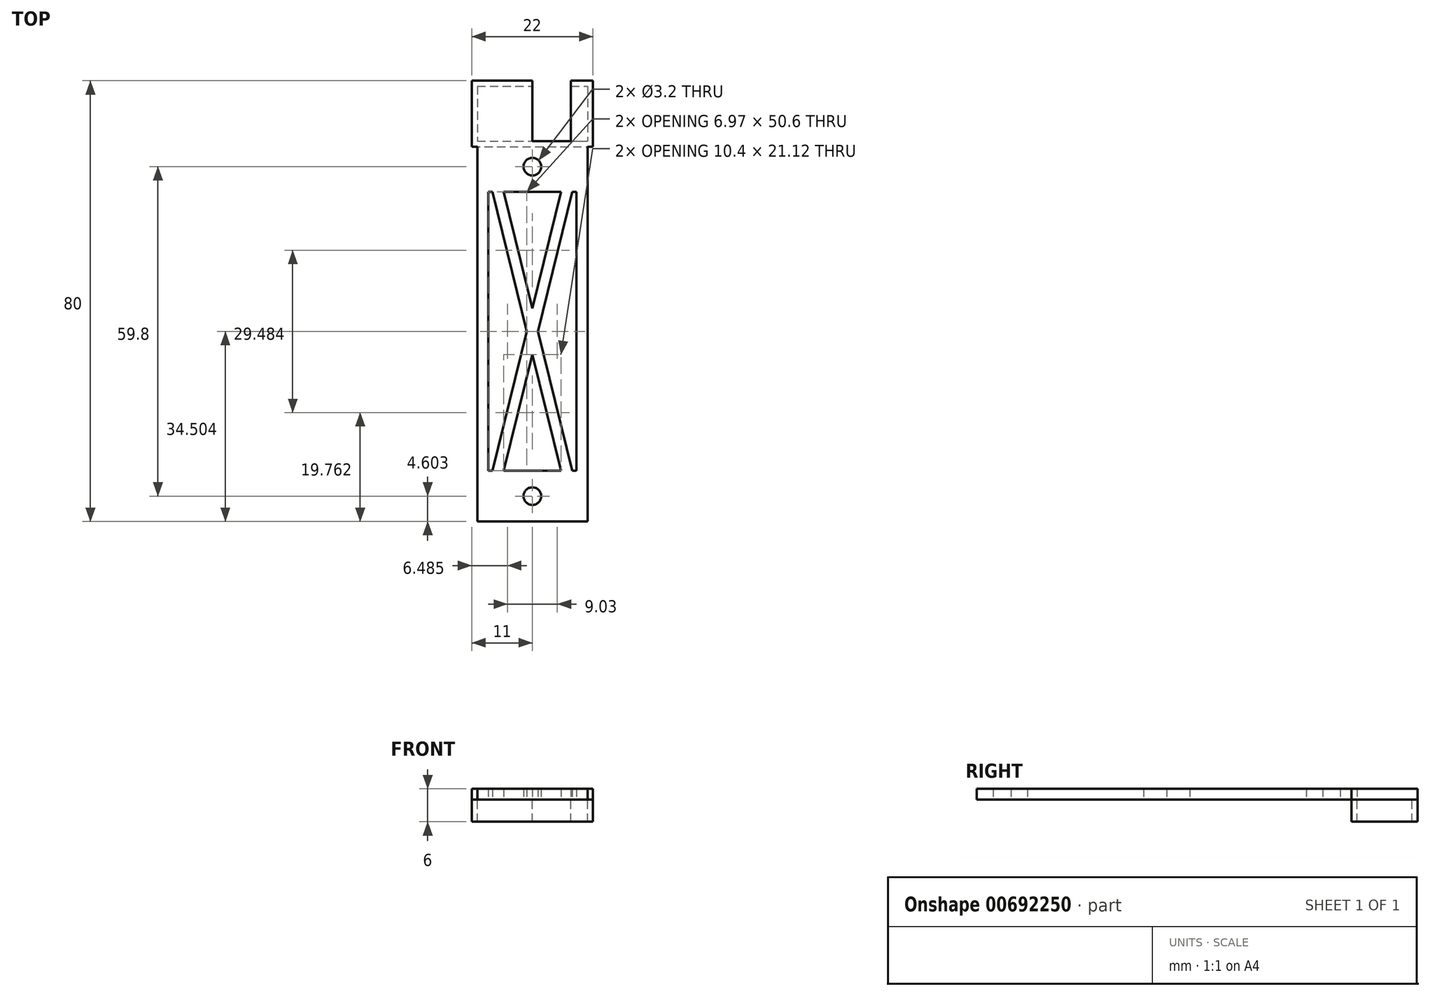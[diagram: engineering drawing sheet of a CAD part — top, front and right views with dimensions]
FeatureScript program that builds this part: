
annotation { "Feature Type Name" : "Feature", "Feature Type Description" : "" }
export const myFeature = defineFeature(function(context is Context, id is Id, definition is map)
    precondition{}
    {
        {
            var Q0;
            Q0=qCreatedBy(makeId("Top.planeOp"),FACE);
            var sketch = newSketch(context, id + "F0", { "sketchPlane" : qUnion([Q0])});
            skLineSegment(sketch, "E0.bottom", {"start": v(-16.97, 32.6) * mm, "end": v(3.03, 32.6) * mm});
            skLineSegment(sketch, "E0.top", {"start": v(-16.97, -47.4) * mm, "end": v(3.03, -47.4) * mm});
            skLineSegment(sketch, "E0.left", {"start": v(-16.97, 32.6) * mm, "end": v(-16.97, -47.4) * mm});
            skLineSegment(sketch, "E0.right", {"start": v(3.03, 32.6) * mm, "end": v(3.03, -47.4) * mm});
            skLineSegment(sketch, "E1", {"start": v(-6.97, 32.6) * mm, "end": v(-6.97, -47.4) * mm});
            skCircle(sketch, "E2", {"center": v(-6.97, -42.8) * mm, "radius": 1.6 * mm});
            skCircle(sketch, "E3", {"center": v(-6.97, 17) * mm, "radius": 1.6 * mm});
            skLineSegment(sketch, "E4", {"start": v(-16.97, 21.6) * mm, "end": v(3.03, 21.6) * mm});
            skLineSegment(sketch, "E5", {"start": v(-16.97, 31.6) * mm, "end": v(3.03, 31.6) * mm});
            skLineSegment(sketch, "E6", {"start": v(-16.97, 20.6) * mm, "end": v(3.03, 20.6) * mm});
            skLineSegment(sketch, "E7", {"start": v(-16.97, 32.6) * mm, "end": v(-17.97, 32.6) * mm});
            skLineSegment(sketch, "E8", {"start": v(-16.97, 20.6) * mm, "end": v(-17.97, 20.6) * mm});
            skLineSegment(sketch, "E9", {"start": v(-17.97, 32.6) * mm, "end": v(-17.97, 20.6) * mm});
            skLineSegment(sketch, "E10", {"start": v(3.03, 32.6) * mm, "end": v(4.03, 32.6) * mm});
            skLineSegment(sketch, "E11", {"start": v(3.03, 20.6) * mm, "end": v(4.03, 20.6) * mm});
            skLineSegment(sketch, "E12", {"start": v(4.03, 32.6) * mm, "end": v(4.03, 20.6) * mm});
            skLineSegment(sketch, "E13", {"start": v(0.03, 32.6) * mm, "end": v(0.03, 21.6) * mm});
            skLineSegment(sketch, "E14", {"start": v(-14.97, 19.6) * mm, "end": v(-14.97, -45.4) * mm});
            skLineSegment(sketch, "E15", {"start": v(-14.97, -45.4) * mm, "end": v(1.03, -45.4) * mm});
            skLineSegment(sketch, "E16", {"start": v(1.03, -45.4) * mm, "end": v(1.03, 19.6) * mm});
            skLineSegment(sketch, "E17", {"start": v(1.03, 19.6) * mm, "end": v(-14.97, 19.6) * mm});
            skLineSegment(sketch, "E18", {"start": v(-14.97, 19.6) * mm, "end": v(1.03, -45.4) * mm});
            skLineSegment(sketch, "E19", {"start": v(1.03, 19.6) * mm, "end": v(-14.97, -45.4) * mm});
            skLineSegment(sketch, "E20", {"start": v(-13.94, 19.6) * mm, "end": v(1.03, -41.21) * mm});
            skLineSegment(sketch, "E21", {"start": v(-14.97, 15.42) * mm, "end": v(0, -45.4) * mm});
            skLineSegment(sketch, "E22", {"start": v(0, 19.6) * mm, "end": v(-14.97, -41.21) * mm});
            skLineSegment(sketch, "E23", {"start": v(1.03, 15.42) * mm, "end": v(-13.94, -45.4) * mm});
            skLineSegment(sketch, "E24", {"start": v(-14.97, -38.2) * mm, "end": v(1.03, -38.2) * mm});
            skLineSegment(sketch, "E25", {"start": v(-14.97, 12.4) * mm, "end": v(1.03, 12.4) * mm});
            skSolve(sketch);
        }
        {
            var Q0;
            {var subQ1=sQuery(id+"F0.wireOp",EDGE,"E0.bottom");var subQ3=sQuery(id+"F0.wireOp",EDGE,"E1");var subQ4=makeQuery(id+"F0.imprint","INTERSECT",VERTEX,{"derivedFrom":[subQ1,subQ3]});Q0=makeQuery(id+"F0.imprint","IMPRINT",FACE,{"disambiguationData":[TD([[makeQuery(id+"F0.imprint","IMPRINT",EDGE,{"disambiguationData":[TD([[subQ4,-1.0]])],"derivedFrom":subQ3}),-1.0]])]});}
            var Q1;
            {var subQ0=sQuery(id+"F0.wireOp",EDGE,"E0.right");var subQ5=sQuery(id+"F0.wireOp",EDGE,"E5");var subQ6=makeQuery(id+"F0.imprint","INTERSECT",VERTEX,{"derivedFrom":[subQ0,subQ5]});Q1=makeQuery(id+"F0.imprint","IMPRINT",FACE,{"disambiguationData":[TD([[makeQuery(id+"F0.imprint","IMPRINT",EDGE,{"disambiguationData":[TD([[subQ6,1.0]])],"derivedFrom":subQ5}),1.0]])]});}
            var Q2;
            {var subQ0=sQuery(id+"F0.wireOp",EDGE,"E7");Q2=makeQuery(id+"F0.imprint","IMPRINT",FACE,{"disambiguationData":[TD([[makeQuery(id+"F0.imprint","IMPRINT",EDGE,{"derivedFrom":subQ0}),1.0]])]});}
            var Q3;
            {var subQ0=sQuery(id+"F0.wireOp",EDGE,"E10");Q3=makeQuery(id+"F0.imprint","IMPRINT",FACE,{"disambiguationData":[TD([[makeQuery(id+"F0.imprint","IMPRINT",EDGE,{"derivedFrom":subQ0}),-1.0]])]});}
            var Q4;
            {var subQ8=sQuery(id+"F0.wireOp",EDGE,"E0.left");var subQ9=sQuery(id+"F0.wireOp",EDGE,"E0.top");var subQ10=makeQuery(id+"F0.imprint","INTERSECT",VERTEX,{"derivedFrom":[subQ9,subQ8]});Q4=makeQuery(id+"F0.imprint","IMPRINT",FACE,{"disambiguationData":[TD([[makeQuery(id+"F0.imprint","IMPRINT",EDGE,{"disambiguationData":[TD([[subQ10,-1.0]])],"derivedFrom":subQ9}),1.0]])]});}
            var Q5;
            {var subQ8=sQuery(id+"F0.wireOp",EDGE,"E0.right");var subQ9=sQuery(id+"F0.wireOp",EDGE,"E0.top");var subQ10=makeQuery(id+"F0.imprint","INTERSECT",VERTEX,{"derivedFrom":[subQ9,subQ8]});Q5=makeQuery(id+"F0.imprint","IMPRINT",FACE,{"disambiguationData":[TD([[makeQuery(id+"F0.imprint","IMPRINT",EDGE,{"disambiguationData":[TD([[subQ10,1.0]])],"derivedFrom":subQ9}),1.0]])]});}
            var Q6;
            {var subQ0=sQuery(id+"F0.wireOp",EDGE,"E4");var subQ5=sQuery(id+"F0.wireOp",EDGE,"E1");var subQ6=makeQuery(id+"F0.imprint","INTERSECT",VERTEX,{"derivedFrom":[subQ5,subQ0]});Q6=makeQuery(id+"F0.imprint","IMPRINT",FACE,{"disambiguationData":[TD([[makeQuery(id+"F0.imprint","IMPRINT",EDGE,{"disambiguationData":[TD([[subQ6,-1.0]])],"derivedFrom":subQ5}),-1.0]])]});}
            var Q7;
            {var subQ0=sQuery(id+"F0.wireOp",EDGE,"E4");var subQ4=sQuery(id+"F0.wireOp",EDGE,"E1");var subQ5=makeQuery(id+"F0.imprint","INTERSECT",VERTEX,{"derivedFrom":[subQ4,subQ0]});Q7=makeQuery(id+"F0.imprint","IMPRINT",FACE,{"disambiguationData":[TD([[makeQuery(id+"F0.imprint","IMPRINT",EDGE,{"disambiguationData":[TD([[subQ5,-1.0]])],"derivedFrom":subQ4}),1.0]])]});}
            var Q8;
            {var subQ0=sQuery(id+"F0.wireOp",EDGE,"E4");var subQ1=sQuery(id+"F0.wireOp",EDGE,"E0.left");var subQ2=makeQuery(id+"F0.imprint","INTERSECT",VERTEX,{"derivedFrom":[subQ1,subQ0]});Q8=makeQuery(id+"F0.imprint","IMPRINT",FACE,{"disambiguationData":[TD([[makeQuery(id+"F0.imprint","IMPRINT",EDGE,{"disambiguationData":[TD([[subQ2,1.0]])],"derivedFrom":subQ1}),1.0]])]});}
            var Q9;
            {var subQ0=sQuery(id+"F0.wireOp",EDGE,"E4");var subQ1=sQuery(id+"F0.wireOp",EDGE,"E0.right");var subQ2=makeQuery(id+"F0.imprint","INTERSECT",VERTEX,{"derivedFrom":[subQ1,subQ0]});Q9=makeQuery(id+"F0.imprint","IMPRINT",FACE,{"disambiguationData":[TD([[makeQuery(id+"F0.imprint","IMPRINT",EDGE,{"disambiguationData":[TD([[subQ2,1.0]])],"derivedFrom":subQ1}),-1.0]])]});}
            var Q10;
            {var subQ1=sQuery(id+"F0.wireOp",EDGE,"E14");var subQ3=sQuery(id+"F0.wireOp",EDGE,"E21");var subQ4=makeQuery(id+"F0.imprint","INTERSECT",VERTEX,{"derivedFrom":[subQ1,subQ3]});Q10=makeQuery(id+"F0.imprint","IMPRINT",FACE,{"disambiguationData":[TD([[makeQuery(id+"F0.imprint","IMPRINT",EDGE,{"disambiguationData":[TD([[subQ4,-1.0]])],"derivedFrom":subQ3}),1.0]])]});}
            var Q11;
            {var subQ1=sQuery(id+"F0.wireOp",EDGE,"E17");var subQ3=sQuery(id+"F0.wireOp",EDGE,"E20");var subQ4=makeQuery(id+"F0.imprint","INTERSECT",VERTEX,{"derivedFrom":[subQ1,subQ3]});Q11=makeQuery(id+"F0.imprint","IMPRINT",FACE,{"disambiguationData":[TD([[makeQuery(id+"F0.imprint","IMPRINT",EDGE,{"disambiguationData":[TD([[subQ4,-1.0]])],"derivedFrom":subQ1}),1.0]])]});}
            var Q12;
            {var subQ1=sQuery(id+"F0.wireOp",EDGE,"E17");var subQ3=sQuery(id+"F0.wireOp",EDGE,"E22");var subQ4=makeQuery(id+"F0.imprint","INTERSECT",VERTEX,{"derivedFrom":[subQ1,subQ3]});Q12=makeQuery(id+"F0.imprint","IMPRINT",FACE,{"disambiguationData":[TD([[makeQuery(id+"F0.imprint","IMPRINT",EDGE,{"disambiguationData":[TD([[subQ4,1.0]])],"derivedFrom":subQ1}),1.0]])]});}
            var Q13;
            {var subQ0=sQuery(id+"F0.wireOp",EDGE,"E19");var subQ5=sQuery(id+"F0.wireOp",EDGE,"E20");var subQ6=makeQuery(id+"F0.imprint","INTERSECT",VERTEX,{"derivedFrom":[subQ0,subQ5]});Q13=makeQuery(id+"F0.imprint","IMPRINT",FACE,{"disambiguationData":[TD([[makeQuery(id+"F0.imprint","IMPRINT",EDGE,{"disambiguationData":[TD([[subQ6,-1.0]])],"derivedFrom":subQ5}),1.0]])]});}
            var Q14;
            {var subQ0=sQuery(id+"F0.wireOp",EDGE,"E19");var subQ5=sQuery(id+"F0.wireOp",EDGE,"E21");var subQ6=makeQuery(id+"F0.imprint","INTERSECT",VERTEX,{"derivedFrom":[subQ0,subQ5]});Q14=makeQuery(id+"F0.imprint","IMPRINT",FACE,{"disambiguationData":[TD([[makeQuery(id+"F0.imprint","IMPRINT",EDGE,{"disambiguationData":[TD([[subQ6,1.0]])],"derivedFrom":subQ5}),-1.0]])]});}
            var Q15;
            {var subQ1=sQuery(id+"F0.wireOp",EDGE,"E15");var subQ3=sQuery(id+"F0.wireOp",EDGE,"E23");var subQ4=makeQuery(id+"F0.imprint","INTERSECT",VERTEX,{"derivedFrom":[subQ1,subQ3]});Q15=makeQuery(id+"F0.imprint","IMPRINT",FACE,{"disambiguationData":[TD([[makeQuery(id+"F0.imprint","IMPRINT",EDGE,{"disambiguationData":[TD([[subQ4,1.0]])],"derivedFrom":subQ1}),1.0]])]});}
            var Q16;
            {var subQ3=sQuery(id+"F0.wireOp",EDGE,"E19");var subQ5=sQuery(id+"F0.wireOp",EDGE,"E21");var subQ6=makeQuery(id+"F0.imprint","INTERSECT",VERTEX,{"derivedFrom":[subQ3,subQ5]});Q16=makeQuery(id+"F0.imprint","IMPRINT",FACE,{"disambiguationData":[TD([[makeQuery(id+"F0.imprint","IMPRINT",EDGE,{"disambiguationData":[TD([[subQ6,1.0]])],"derivedFrom":subQ5}),1.0]])]});}
            var Q17;
            {var subQ0=sQuery(id+"F0.wireOp",EDGE,"E19");var subQ3=sQuery(id+"F0.wireOp",EDGE,"E21");var subQ5=makeQuery(id+"F0.imprint","INTERSECT",VERTEX,{"derivedFrom":[subQ0,subQ3]});Q17=makeQuery(id+"F0.imprint","IMPRINT",FACE,{"disambiguationData":[TD([[makeQuery(id+"F0.imprint","IMPRINT",EDGE,{"disambiguationData":[TD([[subQ5,1.0]])],"derivedFrom":subQ0}),1.0]])]});}
            var Q18;
            {var subQ3=sQuery(id+"F0.wireOp",EDGE,"E19");var subQ5=sQuery(id+"F0.wireOp",EDGE,"E20");var subQ6=makeQuery(id+"F0.imprint","INTERSECT",VERTEX,{"derivedFrom":[subQ3,subQ5]});Q18=makeQuery(id+"F0.imprint","IMPRINT",FACE,{"disambiguationData":[TD([[makeQuery(id+"F0.imprint","IMPRINT",EDGE,{"disambiguationData":[TD([[subQ6,-1.0]])],"derivedFrom":subQ5}),-1.0]])]});}
            var Q19;
            {var subQ0=sQuery(id+"F0.wireOp",EDGE,"E20");var subQ3=sQuery(id+"F0.wireOp",EDGE,"E19");var subQ5=makeQuery(id+"F0.imprint","INTERSECT",VERTEX,{"derivedFrom":[subQ3,subQ0]});Q19=makeQuery(id+"F0.imprint","IMPRINT",FACE,{"disambiguationData":[TD([[makeQuery(id+"F0.imprint","IMPRINT",EDGE,{"disambiguationData":[TD([[subQ5,-1.0]])],"derivedFrom":subQ3}),-1.0]])]});}
            var Q20;
            {var subQ0=sQuery(id+"F0.wireOp",EDGE,"E18");var subQ3=sQuery(id+"F0.wireOp",EDGE,"E23");var subQ5=makeQuery(id+"F0.imprint","INTERSECT",VERTEX,{"derivedFrom":[subQ0,subQ3]});Q20=makeQuery(id+"F0.imprint","IMPRINT",FACE,{"disambiguationData":[TD([[makeQuery(id+"F0.imprint","IMPRINT",EDGE,{"disambiguationData":[TD([[subQ5,1.0]])],"derivedFrom":subQ0}),-1.0]])]});}
            var Q21;
            {var subQ0=sQuery(id+"F0.wireOp",EDGE,"E22");var subQ3=sQuery(id+"F0.wireOp",EDGE,"E18");var subQ5=makeQuery(id+"F0.imprint","INTERSECT",VERTEX,{"derivedFrom":[subQ3,subQ0]});Q21=makeQuery(id+"F0.imprint","IMPRINT",FACE,{"disambiguationData":[TD([[makeQuery(id+"F0.imprint","IMPRINT",EDGE,{"disambiguationData":[TD([[subQ5,-1.0]])],"derivedFrom":subQ3}),1.0]])]});}
            var Q22;
            {var subQ1=sQuery(id+"F0.wireOp",EDGE,"E16");var subQ3=sQuery(id+"F0.wireOp",EDGE,"E20");var subQ4=makeQuery(id+"F0.imprint","INTERSECT",VERTEX,{"derivedFrom":[subQ1,subQ3]});Q22=makeQuery(id+"F0.imprint","IMPRINT",FACE,{"disambiguationData":[TD([[makeQuery(id+"F0.imprint","IMPRINT",EDGE,{"disambiguationData":[TD([[subQ4,1.0]])],"derivedFrom":subQ3}),-1.0]])]});}
            var Q23;
            {var subQ1=sQuery(id+"F0.wireOp",EDGE,"E15");var subQ3=sQuery(id+"F0.wireOp",EDGE,"E21");var subQ4=makeQuery(id+"F0.imprint","INTERSECT",VERTEX,{"derivedFrom":[subQ1,subQ3]});Q23=makeQuery(id+"F0.imprint","IMPRINT",FACE,{"disambiguationData":[TD([[makeQuery(id+"F0.imprint","IMPRINT",EDGE,{"disambiguationData":[TD([[subQ4,-1.0]])],"derivedFrom":subQ1}),1.0]])]});}
            var Q24;
            {var subQ1=sQuery(id+"F0.wireOp",EDGE,"E16");var subQ3=sQuery(id+"F0.wireOp",EDGE,"E23");var subQ4=makeQuery(id+"F0.imprint","INTERSECT",VERTEX,{"derivedFrom":[subQ1,subQ3]});Q24=makeQuery(id+"F0.imprint","IMPRINT",FACE,{"disambiguationData":[TD([[makeQuery(id+"F0.imprint","IMPRINT",EDGE,{"disambiguationData":[TD([[subQ4,-1.0]])],"derivedFrom":subQ3}),-1.0]])]});}
            var Q25;
            {var subQ0=sQuery(id+"F0.wireOp",EDGE,"E25");var subQ1=sQuery(id+"F0.wireOp",EDGE,"E18");var subQ2=makeQuery(id+"F0.imprint","INTERSECT",VERTEX,{"derivedFrom":[subQ1,subQ0]});Q25=makeQuery(id+"F0.imprint","IMPRINT",FACE,{"disambiguationData":[TD([[makeQuery(id+"F0.imprint","IMPRINT",EDGE,{"disambiguationData":[TD([[subQ2,-1.0]])],"derivedFrom":subQ1}),-1.0]])]});}
            var Q26;
            {var subQ0=sQuery(id+"F0.wireOp",EDGE,"E25");var subQ1=sQuery(id+"F0.wireOp",EDGE,"E18");var subQ2=makeQuery(id+"F0.imprint","INTERSECT",VERTEX,{"derivedFrom":[subQ1,subQ0]});Q26=makeQuery(id+"F0.imprint","IMPRINT",FACE,{"disambiguationData":[TD([[makeQuery(id+"F0.imprint","IMPRINT",EDGE,{"disambiguationData":[TD([[subQ2,-1.0]])],"derivedFrom":subQ1}),1.0]])]});}
            var Q27;
            {var subQ0=sQuery(id+"F0.wireOp",EDGE,"E25");var subQ1=sQuery(id+"F0.wireOp",EDGE,"E19");var subQ2=makeQuery(id+"F0.imprint","INTERSECT",VERTEX,{"derivedFrom":[subQ1,subQ0]});Q27=makeQuery(id+"F0.imprint","IMPRINT",FACE,{"disambiguationData":[TD([[makeQuery(id+"F0.imprint","IMPRINT",EDGE,{"disambiguationData":[TD([[subQ2,-1.0]])],"derivedFrom":subQ1}),-1.0]])]});}
            var Q28;
            {var subQ1=sQuery(id+"F0.wireOp",EDGE,"E17");var subQ3=sQuery(id+"F0.wireOp",EDGE,"E1");var subQ4=makeQuery(id+"F0.imprint","INTERSECT",VERTEX,{"derivedFrom":[subQ3,subQ1]});Q28=makeQuery(id+"F0.imprint","IMPRINT",FACE,{"disambiguationData":[TD([[makeQuery(id+"F0.imprint","IMPRINT",EDGE,{"disambiguationData":[TD([[subQ4,-1.0]])],"derivedFrom":subQ3}),1.0]])]});}
            var Q29;
            {var subQ1=sQuery(id+"F0.wireOp",EDGE,"E1");var subQ7=sQuery(id+"F0.wireOp",EDGE,"E17");var subQ9=makeQuery(id+"F0.imprint","INTERSECT",VERTEX,{"derivedFrom":[subQ1,subQ7]});Q29=makeQuery(id+"F0.imprint","IMPRINT",FACE,{"disambiguationData":[TD([[makeQuery(id+"F0.imprint","IMPRINT",EDGE,{"disambiguationData":[TD([[subQ9,-1.0]])],"derivedFrom":subQ1}),-1.0]])]});}
            var Q30;
            {var subQ0=sQuery(id+"F0.wireOp",EDGE,"E21");var subQ1=sQuery(id+"F0.wireOp",EDGE,"E14");var subQ2=makeQuery(id+"F0.imprint","INTERSECT",VERTEX,{"derivedFrom":[subQ1,subQ0]});Q30=makeQuery(id+"F0.imprint","IMPRINT",FACE,{"disambiguationData":[TD([[makeQuery(id+"F0.imprint","IMPRINT",EDGE,{"disambiguationData":[TD([[subQ2,-1.0]])],"derivedFrom":subQ1}),1.0]])]});}
            var Q31;
            {var subQ0=sQuery(id+"F0.wireOp",EDGE,"E23");var subQ1=sQuery(id+"F0.wireOp",EDGE,"E16");var subQ2=makeQuery(id+"F0.imprint","INTERSECT",VERTEX,{"derivedFrom":[subQ1,subQ0]});Q31=makeQuery(id+"F0.imprint","IMPRINT",FACE,{"disambiguationData":[TD([[makeQuery(id+"F0.imprint","IMPRINT",EDGE,{"disambiguationData":[TD([[subQ2,1.0]])],"derivedFrom":subQ1}),1.0]])]});}
            var Q32;
            {var subQ1=sQuery(id+"F0.wireOp",EDGE,"E14");var subQ3=sQuery(id+"F0.wireOp",EDGE,"E22");var subQ4=makeQuery(id+"F0.imprint","INTERSECT",VERTEX,{"derivedFrom":[subQ1,subQ3]});Q32=makeQuery(id+"F0.imprint","IMPRINT",FACE,{"disambiguationData":[TD([[makeQuery(id+"F0.imprint","IMPRINT",EDGE,{"disambiguationData":[TD([[subQ4,1.0]])],"derivedFrom":subQ3}),1.0]])]});}
            var Q33;
            {var subQ0=sQuery(id+"F0.wireOp",EDGE,"E21");var subQ1=sQuery(id+"F0.wireOp",EDGE,"E19");var subQ2=makeQuery(id+"F0.imprint","INTERSECT",VERTEX,{"derivedFrom":[subQ1,subQ0]});Q33=makeQuery(id+"F0.imprint","IMPRINT",FACE,{"disambiguationData":[TD([[makeQuery(id+"F0.imprint","IMPRINT",EDGE,{"disambiguationData":[TD([[subQ2,-1.0]])],"derivedFrom":subQ1}),1.0]])]});}
            var Q34;
            {var subQ0=sQuery(id+"F0.wireOp",EDGE,"E23");var subQ1=sQuery(id+"F0.wireOp",EDGE,"E18");var subQ2=makeQuery(id+"F0.imprint","INTERSECT",VERTEX,{"derivedFrom":[subQ1,subQ0]});Q34=makeQuery(id+"F0.imprint","IMPRINT",FACE,{"disambiguationData":[TD([[makeQuery(id+"F0.imprint","IMPRINT",EDGE,{"disambiguationData":[TD([[subQ2,-1.0]])],"derivedFrom":subQ1}),1.0]])]});}
            var Q35;
            {var subQ0=sQuery(id+"F0.wireOp",EDGE,"E23");var subQ1=sQuery(id+"F0.wireOp",EDGE,"E18");var subQ2=makeQuery(id+"F0.imprint","INTERSECT",VERTEX,{"derivedFrom":[subQ1,subQ0]});Q35=makeQuery(id+"F0.imprint","IMPRINT",FACE,{"disambiguationData":[TD([[makeQuery(id+"F0.imprint","IMPRINT",EDGE,{"disambiguationData":[TD([[subQ2,-1.0]])],"derivedFrom":subQ1}),-1.0]])]});}
            var Q36;
            {var subQ3=sQuery(id+"F0.wireOp",EDGE,"E1");var subQ8=sQuery(id+"F0.wireOp",EDGE,"E24");var subQ9=makeQuery(id+"F0.imprint","INTERSECT",VERTEX,{"derivedFrom":[subQ3,subQ8]});Q36=makeQuery(id+"F0.imprint","IMPRINT",FACE,{"disambiguationData":[TD([[makeQuery(id+"F0.imprint","IMPRINT",EDGE,{"disambiguationData":[TD([[subQ9,-1.0]])],"derivedFrom":subQ3}),1.0]])]});}
            var Q37;
            {var subQ0=sQuery(id+"F0.wireOp",EDGE,"E20");var subQ1=sQuery(id+"F0.wireOp",EDGE,"E16");var subQ2=makeQuery(id+"F0.imprint","INTERSECT",VERTEX,{"derivedFrom":[subQ1,subQ0]});Q37=makeQuery(id+"F0.imprint","IMPRINT",FACE,{"disambiguationData":[TD([[makeQuery(id+"F0.imprint","IMPRINT",EDGE,{"disambiguationData":[TD([[subQ2,-1.0]])],"derivedFrom":subQ1}),1.0]])]});}
            var Q38;
            {var subQ1=sQuery(id+"F0.wireOp",EDGE,"E1");var subQ4=sQuery(id+"F0.wireOp",EDGE,"E24");var subQ5=makeQuery(id+"F0.imprint","INTERSECT",VERTEX,{"derivedFrom":[subQ1,subQ4]});Q38=makeQuery(id+"F0.imprint","IMPRINT",FACE,{"disambiguationData":[TD([[makeQuery(id+"F0.imprint","IMPRINT",EDGE,{"disambiguationData":[TD([[subQ5,-1.0]])],"derivedFrom":subQ1}),-1.0]])]});}
            var Q39;
            {var subQ0=sQuery(id+"F0.wireOp",EDGE,"E22");var subQ1=sQuery(id+"F0.wireOp",EDGE,"E14");var subQ2=makeQuery(id+"F0.imprint","INTERSECT",VERTEX,{"derivedFrom":[subQ1,subQ0]});Q39=makeQuery(id+"F0.imprint","IMPRINT",FACE,{"disambiguationData":[TD([[makeQuery(id+"F0.imprint","IMPRINT",EDGE,{"disambiguationData":[TD([[subQ2,1.0]])],"derivedFrom":subQ1}),1.0]])]});}
            extrude(context, id + "F1", {"entities" : qUnion([Q0, Q1, Q2, Q3, Q4, Q5, Q6, Q7, Q8, Q9, Q10, Q11, Q12, Q13, Q14, Q15, Q16, Q17, Q18, Q19, Q20, Q21, Q22, Q23, Q24, Q25, Q26, Q27, Q28, Q29, Q30, Q31, Q32, Q33, Q34, Q35, Q36, Q37, Q38, Q39]), "depth" : 2 * mm, "offsetDistance" : 25 * mm});
        }
        {
            var Q0;
            {var subQ0=sQuery(id+"F0.wireOp",EDGE,"E10");Q0=makeQuery(id+"F0.imprint","IMPRINT",FACE,{"disambiguationData":[TD([[makeQuery(id+"F0.imprint","IMPRINT",EDGE,{"derivedFrom":subQ0}),-1.0]])]});}
            var Q1;
            {var subQ0=sQuery(id+"F0.wireOp",EDGE,"E0.right");var subQ5=sQuery(id+"F0.wireOp",EDGE,"E5");var subQ6=makeQuery(id+"F0.imprint","INTERSECT",VERTEX,{"derivedFrom":[subQ0,subQ5]});Q1=makeQuery(id+"F0.imprint","IMPRINT",FACE,{"disambiguationData":[TD([[makeQuery(id+"F0.imprint","IMPRINT",EDGE,{"disambiguationData":[TD([[subQ6,1.0]])],"derivedFrom":subQ5}),1.0]])]});}
            var Q2;
            {var subQ0=sQuery(id+"F0.wireOp",EDGE,"E4");var subQ4=sQuery(id+"F0.wireOp",EDGE,"E1");var subQ5=makeQuery(id+"F0.imprint","INTERSECT",VERTEX,{"derivedFrom":[subQ4,subQ0]});Q2=makeQuery(id+"F0.imprint","IMPRINT",FACE,{"disambiguationData":[TD([[makeQuery(id+"F0.imprint","IMPRINT",EDGE,{"disambiguationData":[TD([[subQ5,-1.0]])],"derivedFrom":subQ4}),1.0]])]});}
            var Q3;
            {var subQ0=sQuery(id+"F0.wireOp",EDGE,"E4");var subQ5=sQuery(id+"F0.wireOp",EDGE,"E1");var subQ6=makeQuery(id+"F0.imprint","INTERSECT",VERTEX,{"derivedFrom":[subQ5,subQ0]});Q3=makeQuery(id+"F0.imprint","IMPRINT",FACE,{"disambiguationData":[TD([[makeQuery(id+"F0.imprint","IMPRINT",EDGE,{"disambiguationData":[TD([[subQ6,-1.0]])],"derivedFrom":subQ5}),-1.0]])]});}
            var Q4;
            {var subQ0=sQuery(id+"F0.wireOp",EDGE,"E7");Q4=makeQuery(id+"F0.imprint","IMPRINT",FACE,{"disambiguationData":[TD([[makeQuery(id+"F0.imprint","IMPRINT",EDGE,{"derivedFrom":subQ0}),1.0]])]});}
            var Q5;
            {var subQ1=sQuery(id+"F0.wireOp",EDGE,"E0.bottom");var subQ3=sQuery(id+"F0.wireOp",EDGE,"E1");var subQ4=makeQuery(id+"F0.imprint","INTERSECT",VERTEX,{"derivedFrom":[subQ1,subQ3]});Q5=makeQuery(id+"F0.imprint","IMPRINT",FACE,{"disambiguationData":[TD([[makeQuery(id+"F0.imprint","IMPRINT",EDGE,{"disambiguationData":[TD([[subQ4,-1.0]])],"derivedFrom":subQ3}),-1.0]])]});}
            extrude(context, id + "F2", {"entities" : qUnion([Q0, Q1, Q2, Q3, Q4, Q5]), "oppositeDirection" : true, "depth" : 4 * mm, "offsetDistance" : 25 * mm});
        }
    });
